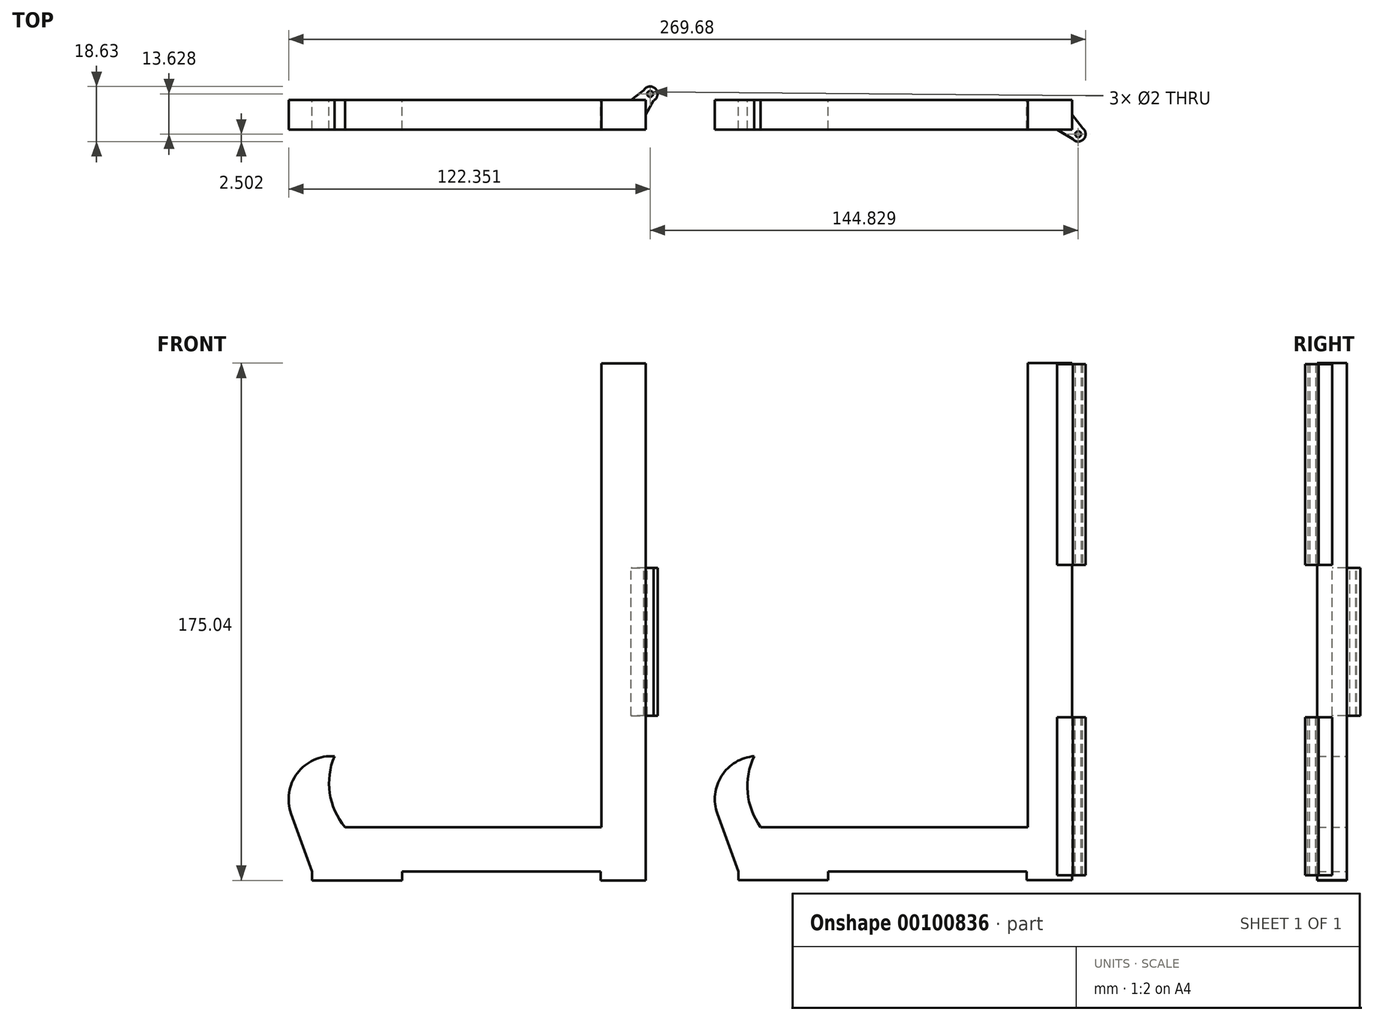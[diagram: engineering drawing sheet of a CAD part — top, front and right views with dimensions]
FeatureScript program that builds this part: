
annotation { "Feature Type Name" : "Feature", "Feature Type Description" : "" }
export const myFeature = defineFeature(function(context is Context, id is Id, definition is map)
    precondition{}
    {
        {
            var Q0;
            Q0=qCreatedBy(makeId("Front.planeOp"),FACE);
            var sketch = newSketch(context, id + "F0", { "sketchPlane" : qUnion([Q0])});
            skLineSegment(sketch, "E0", {"start": v(-13.67, 99.29) * mm, "end": v(1.33, 99.29) * mm});
            skLineSegment(sketch, "E1", {"start": v(1.33, 99.29) * mm, "end": v(1.33, -75.71) * mm});
            skLineSegment(sketch, "E2", {"start": v(1.33, -75.71) * mm, "end": v(-14, -75.71) * mm});
            skLineSegment(sketch, "E3", {"start": v(-14, -75.71) * mm, "end": v(-14, -72.71) * mm});
            skLineSegment(sketch, "E4", {"start": v(-14, -72.71) * mm, "end": v(-111.6, -72.71) * mm});
            skLineSegment(sketch, "E5", {"start": v(-111.6, -72.71) * mm, "end": v(-118.67, -53.2) * mm});
            skLineSegment(sketch, "E6", {"start": v(-104, -57.71) * mm, "end": v(-13.67, -57.71) * mm});
            skLineSegment(sketch, "E7", {"start": v(-13.67, -57.71) * mm, "end": v(-13.67, 99.29) * mm});
            skArc(sketch, "E8", {"start": v(-106.17, -33.72) * mm, "mid": v(-117.23, -40.37) * mm, "end": v(-118.67, -53.2) * mm});
            skLineSegment(sketch, "E9", {"start": v(-111.6, -72.71) * mm, "end": v(-111.6, -75.71) * mm});
            skLineSegment(sketch, "E10", {"start": v(-111.6, -75.71) * mm, "end": v(-81.15, -75.71) * mm});
            skLineSegment(sketch, "E11", {"start": v(-81.15, -75.71) * mm, "end": v(-81.15, -72.71) * mm});
            skLineSegment(sketch, "E12", {"start": v(-14, -72.71) * mm, "end": v(1.33, -72.71) * mm});
            skLineSegment(sketch, "E13", {"start": v(-157.88, 99.25) * mm, "end": v(-142.88, 99.25) * mm});
            skLineSegment(sketch, "E14", {"start": v(-142.88, 99.25) * mm, "end": v(-142.88, -75.75) * mm});
            skLineSegment(sketch, "E15", {"start": v(-142.88, -75.75) * mm, "end": v(-158.2, -75.75) * mm});
            skLineSegment(sketch, "E16", {"start": v(-158.2, -75.75) * mm, "end": v(-158.2, -72.75) * mm});
            skLineSegment(sketch, "E17", {"start": v(-158.2, -72.75) * mm, "end": v(-255.82, -72.75) * mm});
            skLineSegment(sketch, "E18", {"start": v(-255.82, -72.75) * mm, "end": v(-262.88, -53.24) * mm});
            skLineSegment(sketch, "E19", {"start": v(-244.67, -57.75) * mm, "end": v(-157.88, -57.75) * mm});
            skLineSegment(sketch, "E20", {"start": v(-157.88, -57.75) * mm, "end": v(-157.88, 99.25) * mm});
            skArc(sketch, "E21", {"start": v(-248.23, -33.74) * mm, "mid": v(-260.83, -39.52) * mm, "end": v(-262.88, -53.24) * mm});
            skLineSegment(sketch, "E22", {"start": v(-255.82, -72.75) * mm, "end": v(-255.82, -75.75) * mm});
            skLineSegment(sketch, "E23", {"start": v(-255.82, -75.75) * mm, "end": v(-225.36, -75.75) * mm});
            skLineSegment(sketch, "E24", {"start": v(-225.36, -75.75) * mm, "end": v(-225.36, -72.75) * mm});
            skLineSegment(sketch, "E25", {"start": v(-158.2, -72.75) * mm, "end": v(-142.88, -72.75) * mm});
            skLineSegment(sketch, "E26", {"start": v(1.33, 31.92) * mm, "end": v(1.33, -2.68) * mm});
            skLineSegment(sketch, "E27", {"start": v(-142.8, 32.2) * mm, "end": v(-142.8, -17.8) * mm});
            skArc(sketch, "E28", {"start": v(-248.23, -33.74) * mm, "mid": v(-249.82, -46.24) * mm, "end": v(-244.67, -57.75) * mm});
            skArc(sketch, "E29", {"start": v(-106.17, -33.72) * mm, "mid": v(-108.42, -46.02) * mm, "end": v(-104, -57.71) * mm});
            skSolve(sketch);
        }
        {
            var Q0;
            {var subQ3=sQuery(id+"F0.wireOp",EDGE,"E13");Q0=makeQuery(id+"F0.imprint","IMPRINT",FACE,{"disambiguationData":[TD([[makeQuery(id+"F0.imprint","IMPRINT",EDGE,{"derivedFrom":subQ3}),-1.0]])]});}
            var Q1;
            {var subQ0=sQuery(id+"F0.wireOp",EDGE,"E15");Q1=makeQuery(id+"F0.imprint","IMPRINT",FACE,{"disambiguationData":[TD([[makeQuery(id+"F0.imprint","IMPRINT",EDGE,{"derivedFrom":subQ0}),-1.0]])]});}
            var Q2;
            {var subQ6=sQuery(id+"F0.wireOp",EDGE,"E0");Q2=makeQuery(id+"F0.imprint","IMPRINT",FACE,{"disambiguationData":[TD([[makeQuery(id+"F0.imprint","IMPRINT",EDGE,{"derivedFrom":subQ6}),-1.0]])]});}
            var Q3;
            {var subQ0=sQuery(id+"F0.wireOp",EDGE,"E9");Q3=makeQuery(id+"F0.imprint","IMPRINT",FACE,{"disambiguationData":[TD([[makeQuery(id+"F0.imprint","IMPRINT",EDGE,{"derivedFrom":subQ0}),1.0]])]});}
            var Q4;
            {var subQ0=sQuery(id+"F0.wireOp",EDGE,"E2");Q4=makeQuery(id+"F0.imprint","IMPRINT",FACE,{"disambiguationData":[TD([[makeQuery(id+"F0.imprint","IMPRINT",EDGE,{"derivedFrom":subQ0}),-1.0]])]});}
            var Q5;
            {var subQ0=sQuery(id+"F0.wireOp",EDGE,"E22");Q5=makeQuery(id+"F0.imprint","IMPRINT",FACE,{"disambiguationData":[TD([[makeQuery(id+"F0.imprint","IMPRINT",EDGE,{"derivedFrom":subQ0}),1.0]])]});}
            extrude(context, id + "F1", {"entities" : qUnion([Q0, Q1, Q2, Q3, Q4, Q5]), "endBound" : BoundingType.SYMMETRIC, "depth" : 10 * mm});
        }
        {
            var Q0;
            Q0=qCreatedBy(makeId("Top.planeOp"),FACE);
            var sketch = newSketch(context, id + "F2", { "sketchPlane" : qUnion([Q0])});
            skCircle(sketch, "E30", {"center": v(3.43, -6.6) * mm, "radius": 2.5 * mm});
            skCircle(sketch, "E31", {"center": v(3.43, -6.6) * mm, "radius": 1 * mm});
            skCircle(sketch, "E32", {"center": v(-141.4, 7.03) * mm, "radius": 2.5 * mm});
            skCircle(sketch, "E33", {"center": v(-141.4, 7.03) * mm, "radius": 1 * mm});
            skLineSegment(sketch, "E34", {"start": v(-147.88, 4.99) * mm, "end": v(-143.56, 8.28) * mm});
            skLineSegment(sketch, "E35", {"start": v(-140.3, 4.78) * mm, "end": v(-142.88, 0) * mm});
            skLineSegment(sketch, "E36", {"start": v(-142.88, 0) * mm, "end": v(-147.88, 4.99) * mm});
            skLineSegment(sketch, "E37", {"start": v(-3.67, -5.02) * mm, "end": v(1.56, -8.26) * mm});
            skLineSegment(sketch, "E38", {"start": v(4.89, -4.57) * mm, "end": v(1.31, 0) * mm});
            skLineSegment(sketch, "E39", {"start": v(1.31, 0) * mm, "end": v(-3.67, -5.02) * mm});
            skLineSegment(sketch, "E40", {"start": v(-3.67, -5.02) * mm, "end": v(1.52, -8.2) * mm});
            skSolve(sketch);
        }
        {
            var Q0;
            Q0=makeQuery(id+"F2.imprint","IMPRINT",FACE,{"disambiguationData":[TD([[makeQuery(id+"F2.imprint","IMPRINT",EDGE,{"derivedFrom":sQuery(id+"F2.wireOp",EDGE,"E33")}),-1.0]])]});
            var Q1;
            {var subQ1=sQuery(id+"F2.wireOp",EDGE,"E34");Q1=makeQuery(id+"F2.imprint","IMPRINT",FACE,{"disambiguationData":[TD([[makeQuery(id+"F2.imprint","IMPRINT",EDGE,{"derivedFrom":subQ1}),-1.0]])]});}
            extrude(context, id + "F3", {"entities" : qUnion([Q0, Q1]), "operationType" : NewBodyOperationType.ADD, "oppositeDirection" : true, "depth" : 20 * mm, "hasSecondDirection" : true, "secondDirectionOppositeDirection" : false, "secondDirectionDepth" : 30 * mm});
        }
        {
            var Q0;
            {var subQ0=sQuery(id+"F2.wireOp",EDGE,"E30");var subQ1=sQuery(id+"F2.wireOp",EDGE,"E30");var subQ2=makeQuery(id+"F2.imprint","INTERSECT",VERTEX,{"disambiguationData":[OD(0.0)],"derivedFrom":[subQ1,subQ0]});Q0=makeQuery(id+"F2.imprint","IMPRINT",FACE,{"disambiguationData":[TD([[makeQuery(id+"F2.imprint","IMPRINT",EDGE,{"disambiguationData":[TD([[subQ2,-1.0]])],"derivedFrom":subQ1}),1.0]])]});}
            var Q1;
            Q1=makeQuery(id+"F2.imprint","IMPRINT",FACE,{"disambiguationData":[TD([[makeQuery(id+"F2.imprint","IMPRINT",EDGE,{"derivedFrom":sQuery(id+"F2.wireOp",EDGE,"E30")}),1.0]])]});
            var Q2;
            {var subQ3=sQuery(id+"F2.wireOp",EDGE,"E30");var subQ6=sQuery(id+"F2.wireOp",EDGE,"nEcuQUTC-MZRc-RGwF-He4q-icZNnftnIZbc");var subQ9=makeQuery(id+"F2.imprint","INTERSECT",VERTEX,{"derivedFrom":[subQ3,subQ6]});Q2=makeQuery(id+"F2.imprint","IMPRINT",FACE,{"disambiguationData":[TD([[makeQuery(id+"F2.imprint","IMPRINT",EDGE,{"disambiguationData":[TD([[subQ9,-1.0]])],"derivedFrom":subQ3}),-1.0]])]});}
            var Q3;
            Q3=makeQuery(id+"F2.imprint","IMPRINT",FACE,{"disambiguationData":[TD([[makeQuery(id+"F2.imprint","IMPRINT",EDGE,{"derivedFrom":sQuery(id+"F2.wireOp",EDGE,"E31")}),-1.0]])]});
            var Q4;
            {var subQ0=sQuery(id+"F2.wireOp",EDGE,"E40");Q4=makeQuery(id+"F2.imprint","IMPRINT",FACE,{"disambiguationData":[TD([[makeQuery(id+"F2.imprint","IMPRINT",EDGE,{"derivedFrom":subQ0}),1.0]])]});}
            extrude(context, id + "F4", {"entities" : qUnion([Q0, Q1, Q2, Q3, Q4]), "operationType" : NewBodyOperationType.ADD, "oppositeDirection" : true, "depth" : 74 * mm, "hasSecondDirection" : true, "secondDirectionOppositeDirection" : true, "secondDirectionDepth" : 20.5 * mm});
        }
        {
            var Q0;
            Q0=makeQuery(id+"F2.imprint","IMPRINT",FACE,{"disambiguationData":[TD([[makeQuery(id+"F2.imprint","IMPRINT",EDGE,{"derivedFrom":sQuery(id+"F2.wireOp",EDGE,"E31")}),-1.0]])]});
            var Q1;
            {var subQ3=sQuery(id+"F2.wireOp",EDGE,"E30");var subQ6=sQuery(id+"F2.wireOp",EDGE,"nEcuQUTC-MZRc-RGwF-He4q-icZNnftnIZbc");var subQ9=makeQuery(id+"F2.imprint","INTERSECT",VERTEX,{"derivedFrom":[subQ3,subQ6]});Q1=makeQuery(id+"F2.imprint","IMPRINT",FACE,{"disambiguationData":[TD([[makeQuery(id+"F2.imprint","IMPRINT",EDGE,{"disambiguationData":[TD([[subQ9,-1.0]])],"derivedFrom":subQ3}),-1.0]])]});}
            var Q2;
            {var subQ0=sQuery(id+"F2.wireOp",EDGE,"E40");Q2=makeQuery(id+"F2.imprint","IMPRINT",FACE,{"disambiguationData":[TD([[makeQuery(id+"F2.imprint","IMPRINT",EDGE,{"derivedFrom":subQ0}),1.0]])]});}
            extrude(context, id + "F5", {"entities" : qUnion([Q0, Q1, Q2]), "operationType" : NewBodyOperationType.ADD, "depth" : 99 * mm, "hasSecondDirection" : true, "secondDirectionOppositeDirection" : false, "secondDirectionDepth" : 31 * mm});
        }
    });
